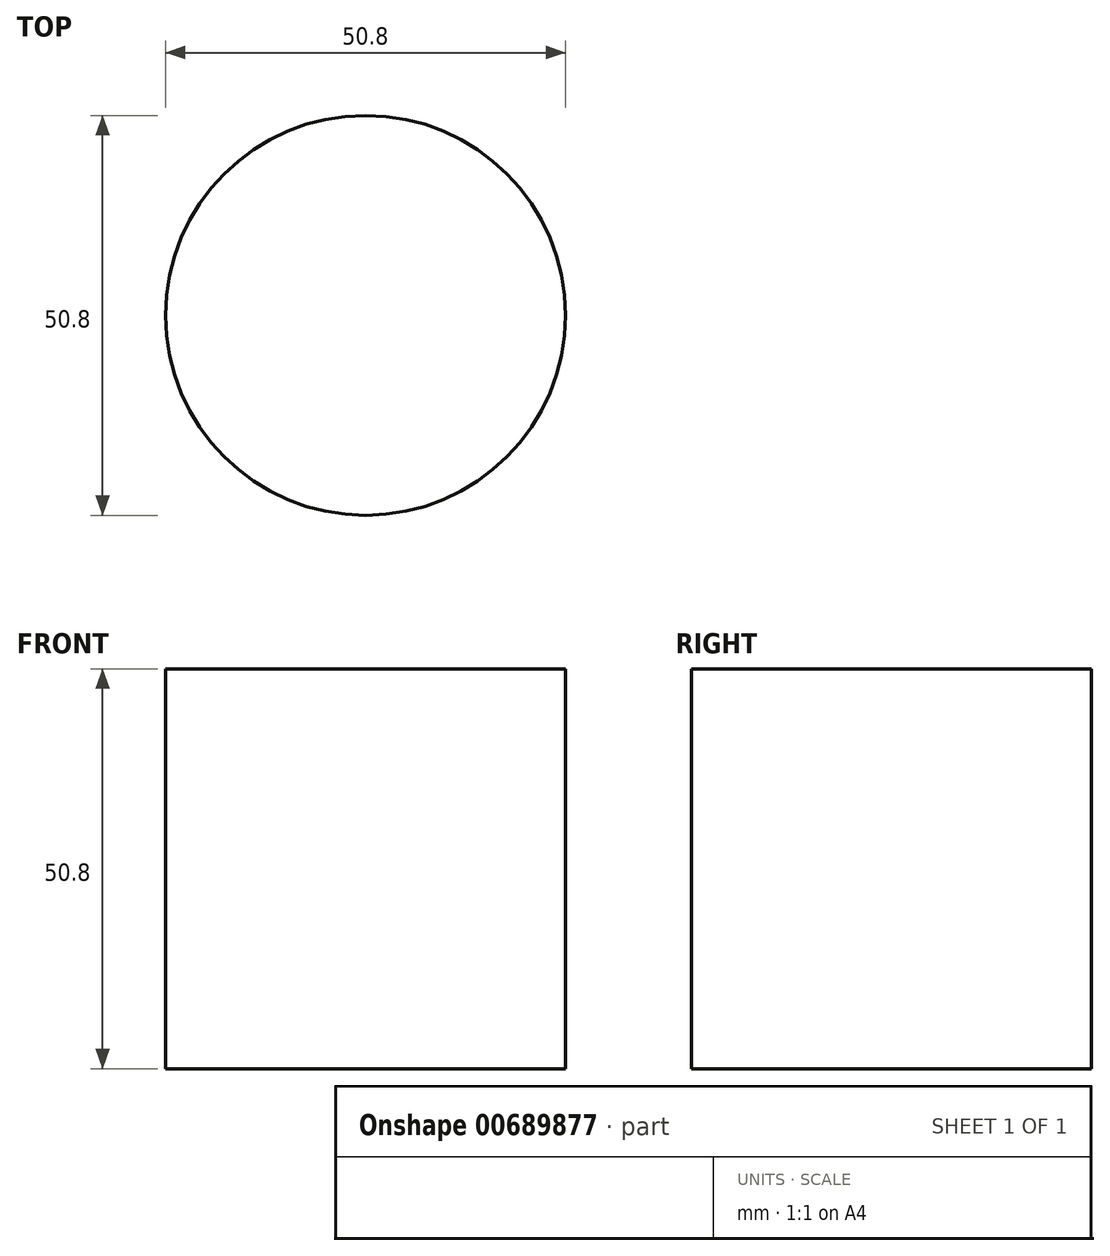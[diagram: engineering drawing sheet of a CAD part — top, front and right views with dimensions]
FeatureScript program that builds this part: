
annotation { "Feature Type Name" : "Feature", "Feature Type Description" : "" }
export const myFeature = defineFeature(function(context is Context, id is Id, definition is map)
    precondition{}
    {
        {
            var Q0;
            Q0=qCreatedBy(makeId("Top.planeOp"),FACE);
            var sketch = newSketch(context, id + "F0", { "sketchPlane" : qUnion([Q0])});
            skLineSegment(sketch, "E0", {"start": v(-73.71, 39.08) * mm, "end": v(-67.94, 35.02) * mm});
            skCircle(sketch, "E1", {"center": v(0, 0) * mm, "radius": 25.4 * mm});
            skSolve(sketch);
        }
        {
            var Q0;
            Q0 = qSketchRegion(id + "F0", true);
            extrude(context, id + "F1", {"entities" : qUnion([Q0]), "depth" : 50.8 * mm, "offsetDistance" : 25.4 * mm});
        }
    });
